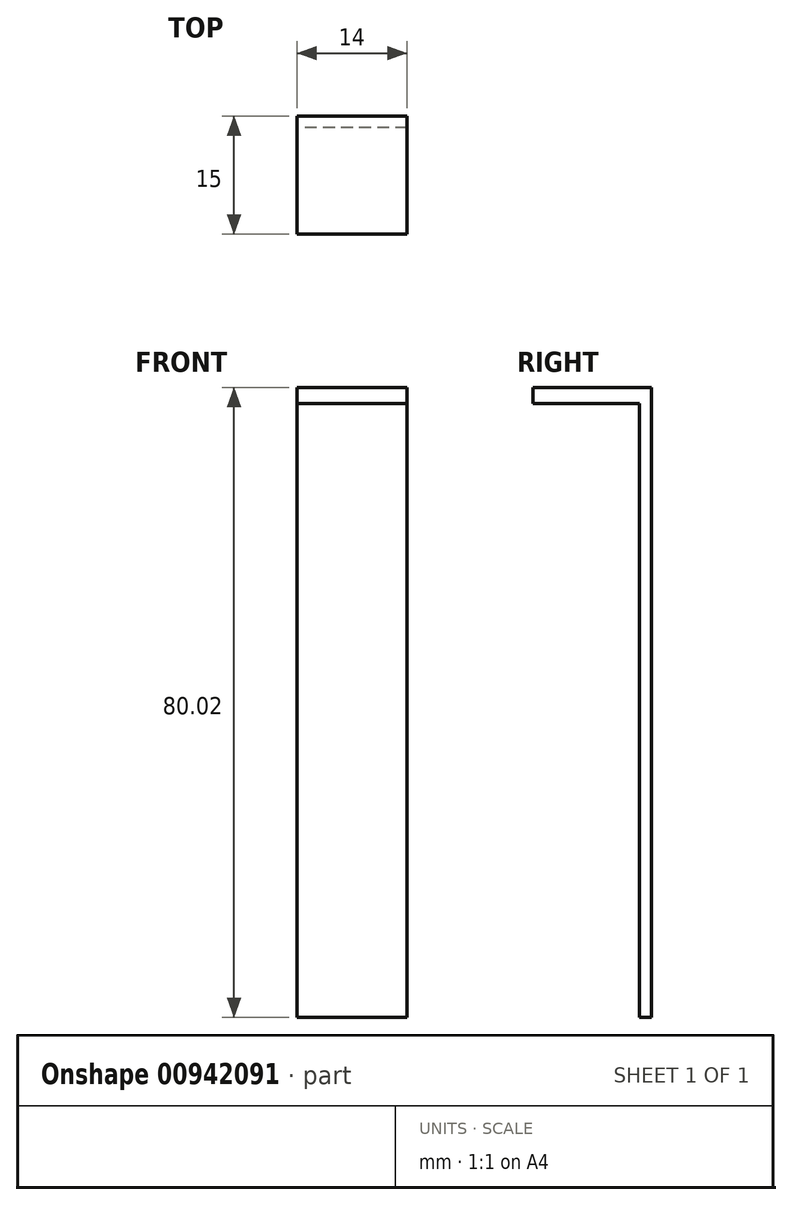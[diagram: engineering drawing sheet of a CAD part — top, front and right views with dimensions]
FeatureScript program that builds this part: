
annotation { "Feature Type Name" : "Feature", "Feature Type Description" : "" }
export const myFeature = defineFeature(function(context is Context, id is Id, definition is map)
    precondition{}
    {
        {
            var Q0;
            Q0=qCreatedBy(makeId("Front.planeOp"),FACE);
            var sketch = newSketch(context, id + "F0", { "sketchPlane" : qUnion([Q0])});
            skLineSegment(sketch, "E0.bottom", {"start": v(0, 43.57) * mm, "end": v(-14, 43.57) * mm});
            skLineSegment(sketch, "E0.top", {"start": v(0, -36.43) * mm, "end": v(-14, -36.43) * mm});
            skLineSegment(sketch, "E0.left", {"start": v(0, 43.57) * mm, "end": v(0, -36.43) * mm});
            skLineSegment(sketch, "E0.right", {"start": v(-14, 43.57) * mm, "end": v(-14, -36.43) * mm});
            skPoint(sketch, "E0.middle", {"position": v(-7, 3.57) * mm});
            skSolve(sketch);
        }
        {
            var Q0;
            Q0 = qSketchRegion(id + "F0", true);
            extrude(context, id + "F1", {"entities" : qUnion([Q0]), "depth" : 1.5 * mm, "offsetDistance" : 25 * mm});
        }
        {
            var Q0;
            Q0=qCreatedBy(makeId("Front.planeOp"),FACE);
            var sketch = newSketch(context, id + "F2", { "sketchPlane" : qUnion([Q0])});
            skLineSegment(sketch, "E1.bottom", {"start": v(-14, 43.59) * mm, "end": v(0, 43.59) * mm});
            skLineSegment(sketch, "E1.top", {"start": v(-14, 41.59) * mm, "end": v(0, 41.59) * mm});
            skLineSegment(sketch, "E1.left", {"start": v(-14, 43.59) * mm, "end": v(-14, 41.59) * mm});
            skLineSegment(sketch, "E1.right", {"start": v(0, 43.59) * mm, "end": v(0, 41.59) * mm});
            skSolve(sketch);
        }
        {
            var Q0;
            Q0 = qSketchRegion(id + "F2", true);
            extrude(context, id + "F3", {"entities" : qUnion([Q0]), "operationType" : NewBodyOperationType.ADD, "depth" : 15 * mm, "offsetDistance" : 25 * mm});
        }
    });
